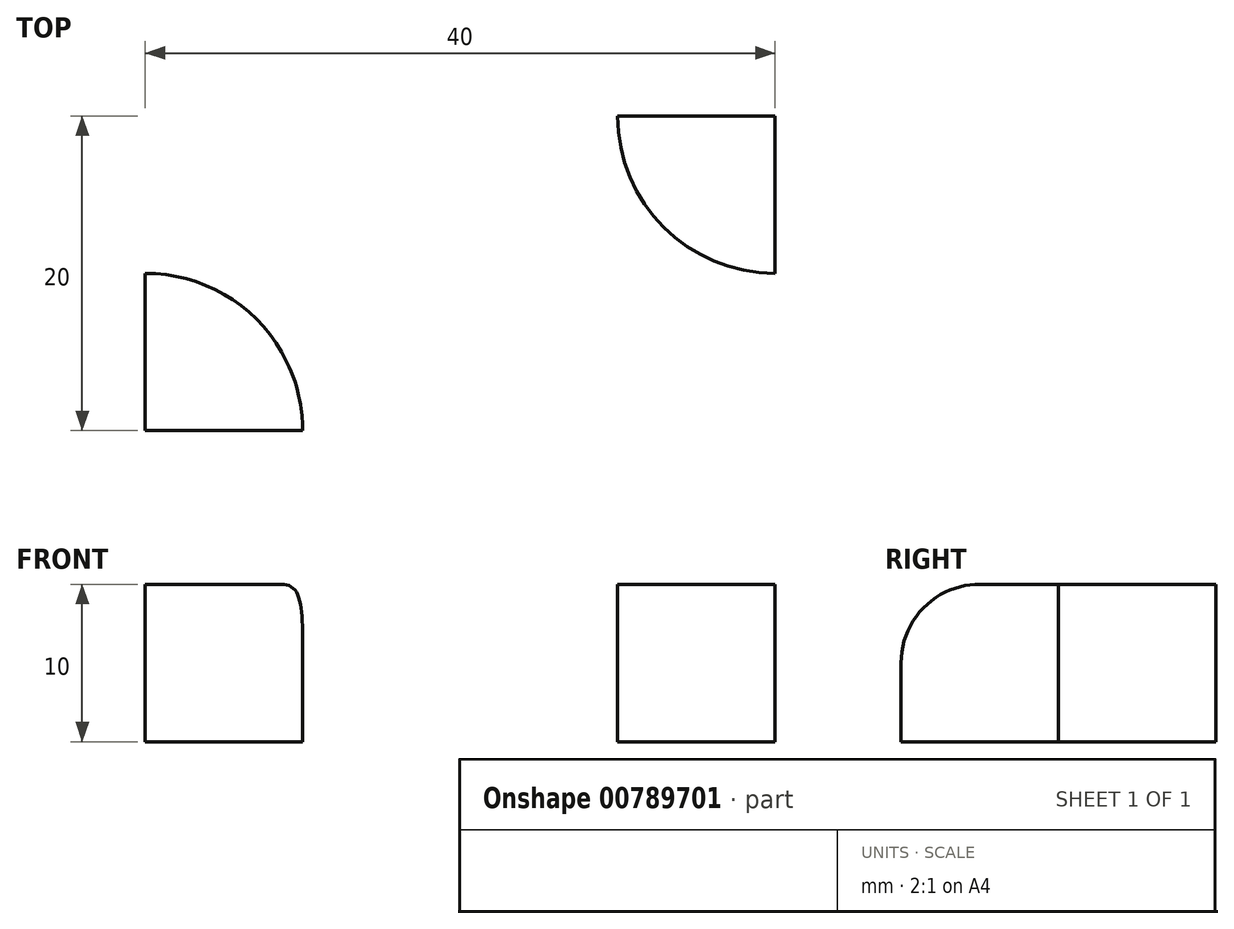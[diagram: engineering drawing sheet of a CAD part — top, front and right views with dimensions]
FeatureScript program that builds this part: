
annotation { "Feature Type Name" : "Feature", "Feature Type Description" : "" }
export const myFeature = defineFeature(function(context is Context, id is Id, definition is map)
    precondition{}
    {
        {
            var Q0;
            Q0=qCreatedBy(makeId("Top.planeOp"),FACE);
            var sketch = newSketch(context, id + "F0", { "sketchPlane" : qUnion([Q0])});
            skLineSegment(sketch, "E0.bottom", {"start": v(20, -10) * mm, "end": v(-20, -10) * mm});
            skLineSegment(sketch, "E0.top", {"start": v(20, 10) * mm, "end": v(-20, 10) * mm});
            skLineSegment(sketch, "E0.left", {"start": v(20, -10) * mm, "end": v(20, 10) * mm});
            skLineSegment(sketch, "E0.right", {"start": v(-20, -10) * mm, "end": v(-20, 10) * mm});
            skPoint(sketch, "E0.middle", {"position": v(0, 0) * mm});
            skSolve(sketch);
        }
        {
            var Q0;
            Q0 = qSketchRegion(id + "F0", true);
            extrude(context, id + "F1", {"entities" : qUnion([Q0]), "depth" : 10 * mm, "offsetDistance" : 25 * mm});
        }
        {
            var Q0;
            Q0=makeQuery(id+"F1.opExtrude","CAP_FACE",FACE,{"disambiguationData":[OSD([sQuery(id+"F0.wireOp",EDGE,"E0.bottom"),sQuery(id+"F0.wireOp",EDGE,"E0.top"),sQuery(id+"F0.wireOp",EDGE,"E0.left"),sQuery(id+"F0.wireOp",EDGE,"E0.right")])],"isStart":false});
            var sketch = newSketch(context, id + "F2", { "sketchPlane" : qUnion([Q0])});
            skArc(sketch, "E1", {"start": v(-20, 0) * mm, "mid": v(-12.93, -2.93) * mm, "end": v(-10, -10) * mm});
            skArc(sketch, "E2", {"start": v(20, 0) * mm, "mid": v(12.93, 2.93) * mm, "end": v(10, 10) * mm});
            skCircle(sketch, "E3.cCircle", {"center": v(0, 0) * mm, "radius": 6.93 * mm, "construction": true});
            skLineSegment(sketch, "E3.0", {"start": v(6.93, -4) * mm, "end": v(0, -8) * mm});
            skLineSegment(sketch, "E3.1", {"start": v(0, -8) * mm, "end": v(-6.93, -4) * mm});
            skLineSegment(sketch, "E3.2", {"start": v(-6.93, -4) * mm, "end": v(-6.93, 4) * mm});
            skLineSegment(sketch, "E3.3", {"start": v(-6.93, 4) * mm, "end": v(0, 8) * mm});
            skLineSegment(sketch, "E3.4", {"start": v(0, 8) * mm, "end": v(6.93, 4) * mm});
            skLineSegment(sketch, "E3.5", {"start": v(6.93, 4) * mm, "end": v(6.93, -4) * mm});
            skPoint(sketch, "E3.0.midPoint", {"position": v(3.46, -6) * mm});
            skSolve(sketch);
        }
        {
            var Q0;
            Q0 = qSketchRegion(id + "F2", true);
            var Q1;
            {var subQ0=sQuery(id+"F2.wireOp",EDGE,"E1");Q1=makeQuery(id+"F2.imprint","IMPRINT",FACE,{"disambiguationData":[TD([[makeQuery(id+"F2.imprint","IMPRINT",EDGE,{"derivedFrom":subQ0}),-1.0]])]});}
            var Q2;
            {var subQ0=sQuery(id+"F2.wireOp",EDGE,"E2");Q2=makeQuery(id+"F2.imprint","IMPRINT",FACE,{"disambiguationData":[TD([[makeQuery(id+"F2.imprint","IMPRINT",EDGE,{"derivedFrom":subQ0}),-1.0]])]});}
            extrude(context, id + "F3", {"entities" : qUnion([Q0, Q1, Q2]), "operationType" : NewBodyOperationType.REMOVE, "oppositeDirection" : true, "depth" : 25 * mm, "offsetDistance" : 25 * mm});
        }
        {
            var Q0;
            Q0=makeQuery(id+"F1.opExtrude","CAP_FACE",FACE,{"disambiguationData":[OSD([sQuery(id+"F0.wireOp",EDGE,"E0.bottom"),sQuery(id+"F0.wireOp",EDGE,"E0.top"),sQuery(id+"F0.wireOp",EDGE,"E0.left"),sQuery(id+"F0.wireOp",EDGE,"E0.right")])],"isStart":false});
            var sketch = newSketch(context, id + "F4", { "sketchPlane" : qUnion([Q0])});
            skLineSegment(sketch, "E4", {"start": v(-20, 10) * mm, "end": v(20, -10) * mm, "construction": true});
            skPoint(sketch, "E5", {"position": v(-14.63, 7.32) * mm});
            skPoint(sketch, "E6", {"position": v(-9.27, 4.63) * mm});
            skSolve(sketch);
        }
        {
            var Q0;
            Q0=sQuery(id+"F4.wireOp",VERTEX,"E5");
            var Q1;
            Q1=sQuery(id+"F4.wireOp",VERTEX,"E6");
            var Q2;
            Q2=makeQuery(id+"F1.opExtrude","SWEPT_BODY",BODY,{"disambiguationData":[OSD([sQuery(id+"F0.wireOp",EDGE,"E0.bottom"),sQuery(id+"F0.wireOp",EDGE,"E0.top"),sQuery(id+"F0.wireOp",EDGE,"E0.left"),sQuery(id+"F0.wireOp",EDGE,"E0.right")])]});
            hole(context, id + "F5", {"style" : HoleStyle.C_SINK, "endStyle" : HoleEndStyle.THROUGH, "standardTappedOrClearance" : lookupTablePath({ "standard" : "ISO", "fit" : "Normal", "size" : "M3", "type" : "Clearance" }), "standardBlindInLast" : lookupTablePath({ "fit" : "Standard", "standard" : "ISO", "size" : "M3", "type" : "Clearance" }), "holeDiameter" : 3.3 * mm, "cSinkDiameter" : 6.72 * mm, "cSinkAngle" : 90 * degree, "majorDiameter" : 5 * mm, "isTappedThrough" : true, "tappedDepth" : 12 * mm, "tapClearance" : 3, "locations" : qUnion([Q0, Q1]), "scope" : qUnion([Q2])});
        }
        {
            var Q0;
            Q0=makeQuery(id+"F1.opExtrude","CAP_EDGE",EDGE,{"disambiguationData":[OSD([sQuery(id+"F0.wireOp",EDGE,"E0.bottom")])],"isStart":false});
            fillet(context, id + "F6", {"entities" : qUnion([Q0]), "radius" : 5 * mm, "tangentPropagation" : true, "allowEdgeOverflow" : false});
        }
    });
